# Revit family: SS 1130 SMD
name_source: partatom
category: Lighting Fixtures
revit_build: Autodesk Revit 2017 (Build: 20160225_1515(x64)
units: mm (PartAtom-declared; Revit-internal decimal feet)

## family parameters
Cut with Voids When Loaded = No
Host = Face
Light Source = Yes
Part Type = Normal
Room Calculation Point = No
Round Connector Dimension = Use Diameter
Shared = No

## types (6) — shared parameters
Color Filter = 16777215
Default Elevation = 1219 mm
Dimming Lamp Color Temperature Shift = <None>
Emit Shape Visible in Rendering = Yes
Emit from Rectangle Length = 49 mm  [stored 0.160761 ft]
Emit from Rectangle Width = 1121 mm  [stored 3.67782 ft]
Lamp = LED
Manufacturer = ARLIGHT
Model = SS1130SMD
Tilt Angle = 90.00°

## per-type parameters (varying)
| type | Apparent Load | Description | Photometric Web File | Type Comments | Type Image | Wattage Comments |
| SSSMD.1130.31.30 | 31 VA |  | SS 1130 SMD-31W-3K(SG-200mA).IES | PENDANT - MICRO LENS (DIRECT) | <None> | 31 |
| SSSMD.1130.31.40 | 31 VA | PENDANT - MICRO LENS (DIRECT) | SS 1130 SMD-31W-4K(SG-200mA).IES | STELLA-START | <None> | 31 |
| SSSMD.1130.18.40 | 18 VA | PENDANT - MICRO LENS (DIRECT) | SS 1130 SMD-18W-4K(SG-120mA).IES | STELLA-START | <None> | 18 |
| SSSMD.1130.18.30 | 18 VA | PENDANT - MICRO LENS (DIRECT) | SS 1130 SMD-18W-3K(SG-120mA).IES | STELLA-START | <None> | 18 |
| SSSMD.1130.51.30 | 51 VA | PENDANT - MICRO LENS (DIRECT) | SS 1130 SMD-51W-3K(SG-350mA).IES | STELLA-START | <None> | 51 |
| SSSMD.1130.51.40 | 51 VA | PENDANT - MICRO LENS (DIRECT) | SS 1130 SMD-51W-4K(SG-350mA).IES | STELLA-START | stella_black_pendant.png | 51 |

note: [stored X ft] marks values corroborated as IEEE doubles in the binary element streams (Revit-internal decimal feet)

## geometry (parser evidence)
native form markers: Sweep x1
no freeform markers — native parametric forms only
